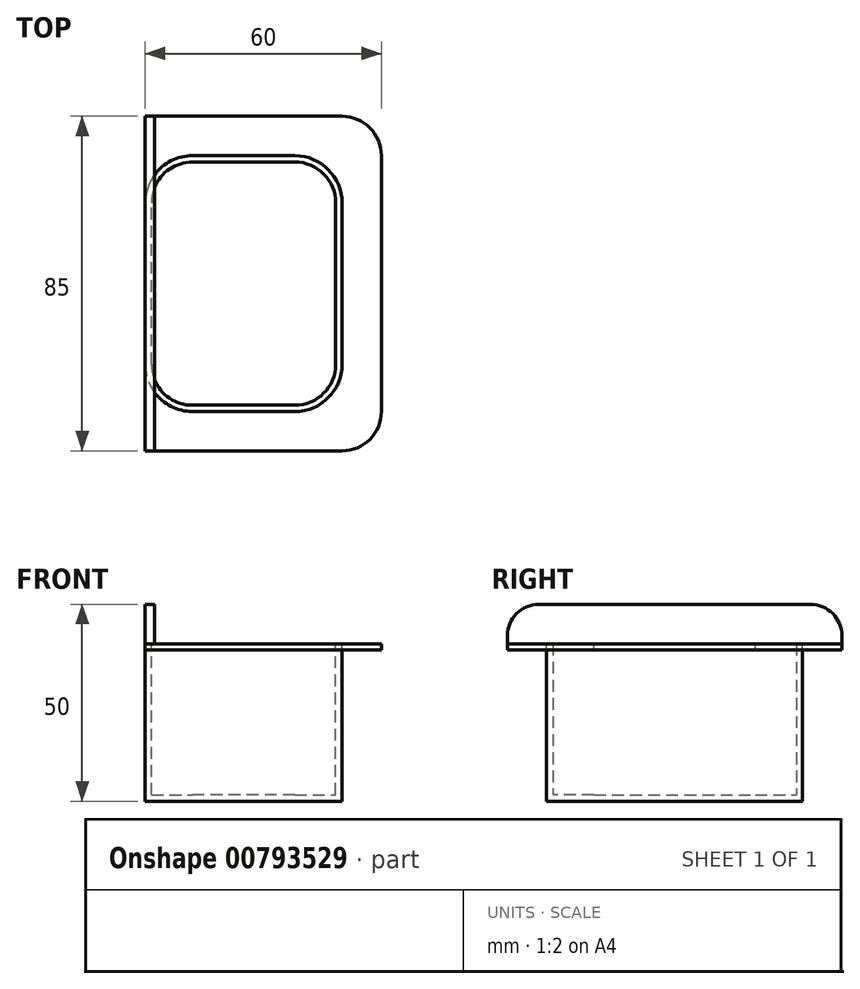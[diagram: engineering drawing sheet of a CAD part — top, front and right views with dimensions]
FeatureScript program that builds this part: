
annotation { "Feature Type Name" : "Feature", "Feature Type Description" : "" }
export const myFeature = defineFeature(function(context is Context, id is Id, definition is map)
    precondition{}
    {
        {
            var Q0;
            Q0=qCreatedBy(makeId("Top.planeOp"),FACE);
            var sketch = newSketch(context, id + "F0", { "sketchPlane" : qUnion([Q0])});
            skLineSegment(sketch, "E0.bottom", {"start": v(25, -32.5) * mm, "end": v(-25, -32.5) * mm});
            skLineSegment(sketch, "E0.top", {"start": v(25, 32.5) * mm, "end": v(-25, 32.5) * mm});
            skLineSegment(sketch, "E0.left", {"start": v(25, -32.5) * mm, "end": v(25, 32.5) * mm});
            skLineSegment(sketch, "E0.right", {"start": v(-25, -32.5) * mm, "end": v(-25, 32.5) * mm});
            skPoint(sketch, "E0.middle", {"position": v(0, 0) * mm});
            skSolve(sketch);
        }
        {
            var Q0;
            Q0 = qSketchRegion(id + "F0", true);
            extrude(context, id + "F1", {"entities" : qUnion([Q0]), "depth" : 40 * mm, "offsetDistance" : 25 * mm});
        }
        {
            var Q0;
            Q0=makeQuery(id+"F1.opExtrude","SWEPT_EDGE",EDGE,{"disambiguationData":[OSD([sQuery(id+"F0.wireOp",EDGE,"E0.bottom"),sQuery(id+"F0.wireOp",EDGE,"E0.right")])]});
            var Q1;
            Q1=makeQuery(id+"F1.opExtrude","SWEPT_EDGE",EDGE,{"disambiguationData":[OSD([sQuery(id+"F0.wireOp",EDGE,"E0.bottom"),sQuery(id+"F0.wireOp",EDGE,"E0.left")])]});
            var Q2;
            Q2=makeQuery(id+"F1.opExtrude","SWEPT_EDGE",EDGE,{"disambiguationData":[OSD([sQuery(id+"F0.wireOp",EDGE,"E0.top"),sQuery(id+"F0.wireOp",EDGE,"E0.left")])]});
            var Q3;
            Q3=makeQuery(id+"F1.opExtrude","SWEPT_EDGE",EDGE,{"disambiguationData":[OSD([sQuery(id+"F0.wireOp",EDGE,"E0.top"),sQuery(id+"F0.wireOp",EDGE,"E0.right")])]});
            fillet(context, id + "F2", {"entities" : qUnion([Q0, Q1, Q2, Q3]), "radius" : 12 * mm, "tangentPropagation" : true, "allowEdgeOverflow" : false});
        }
        {
            var Q0;
            Q0=makeQuery(id+"F1.opExtrude","CAP_FACE",FACE,{"disambiguationData":[OSD([sQuery(id+"F0.wireOp",EDGE,"E0.bottom"),sQuery(id+"F0.wireOp",EDGE,"E0.top"),sQuery(id+"F0.wireOp",EDGE,"E0.left"),sQuery(id+"F0.wireOp",EDGE,"E0.right")])],"isStart":false});
            shell(context, id + "F3", {"entities" : qUnion([Q0]), "thickness" : 1.6 * mm});
        }
        {
            var Q0;
            Q0=makeQuery(id+"F1.opExtrude","CAP_FACE",FACE,{"disambiguationData":[OSD([sQuery(id+"F0.wireOp",EDGE,"E0.bottom"),sQuery(id+"F0.wireOp",EDGE,"E0.top"),sQuery(id+"F0.wireOp",EDGE,"E0.left"),sQuery(id+"F0.wireOp",EDGE,"E0.right")])],"isStart":false});
            var sketch = newSketch(context, id + "F4", { "sketchPlane" : qUnion([Q0])});
            skLineSegment(sketch, "E1.bottom", {"start": v(-25, 42.5) * mm, "end": v(35, 42.5) * mm});
            skLineSegment(sketch, "E1.top", {"start": v(-25, -42.5) * mm, "end": v(35, -42.5) * mm});
            skLineSegment(sketch, "E1.left", {"start": v(-25, 42.5) * mm, "end": v(-25, -42.5) * mm});
            skLineSegment(sketch, "E1.right", {"start": v(35, 42.5) * mm, "end": v(35, -42.5) * mm});
            skSolve(sketch);
        }
        {
            var Q0;
            {var subQ7=sQuery(id+"F4.wireOp",EDGE,"E1.bottom");Q0=makeQuery(id+"F4.imprint","IMPRINT",FACE,{"disambiguationData":[TD([[makeQuery(id+"F4.imprint","IMPRINT",EDGE,{"derivedFrom":subQ7}),-1.0]])]});}
            extrude(context, id + "F5", {"entities" : qUnion([Q0]), "oppositeDirection" : true, "depth" : 1.6 * mm, "offsetDistance" : 25 * mm});
        }
        {
            var Q0;
            Q0=makeQuery(id+"F5.opExtrude","SWEPT_EDGE",EDGE,{"disambiguationData":[OSD([sQuery(id+"F4.wireOp",EDGE,"E1.bottom"),sQuery(id+"F4.wireOp",EDGE,"E1.right")])]});
            var Q1;
            Q1=makeQuery(id+"F5.opExtrude","SWEPT_EDGE",EDGE,{"disambiguationData":[OSD([sQuery(id+"F4.wireOp",EDGE,"E1.top"),sQuery(id+"F4.wireOp",EDGE,"E1.right")])]});
            fillet(context, id + "F6", {"entities" : qUnion([Q0, Q1]), "radius" : 10 * mm, "tangentPropagation" : true, "allowEdgeOverflow" : false});
        }
        {
            var Q0;
            Q0=makeQuery(id+"F5.opExtrude","CAP_FACE",FACE,{"disambiguationData":[OSD([sQuery(id+"F0.wireOp",EDGE,"E0.bottom"),sQuery(id+"F0.wireOp",EDGE,"E0.top"),sQuery(id+"F0.wireOp",EDGE,"E0.left"),sQuery(id+"F0.wireOp",EDGE,"E0.right"),sQuery(id+"F4.wireOp",EDGE,"E1.bottom"),sQuery(id+"F4.wireOp",EDGE,"E1.top"),sQuery(id+"F4.wireOp",EDGE,"E1.left"),sQuery(id+"F4.wireOp",EDGE,"E1.right")])],"isStart":true});
            var sketch = newSketch(context, id + "F7", { "sketchPlane" : qUnion([Q0])});
            skPoint(sketch, "E2.oppositeSnap0", {"position": v(-22.66, -30.16) * mm});
            skLineSegment(sketch, "E2.bottom", {"start": v(-25, 42.5) * mm, "end": v(-22.66, 42.5) * mm});
            skLineSegment(sketch, "E2.top", {"start": v(-25, -42.5) * mm, "end": v(-22.66, -42.5) * mm});
            skLineSegment(sketch, "E2.left", {"start": v(-25, 42.5) * mm, "end": v(-25, -42.5) * mm});
            skLineSegment(sketch, "E2.right", {"start": v(-22.66, 42.5) * mm, "end": v(-22.66, -42.5) * mm});
            skSolve(sketch);
        }
        {
            var Q0;
            Q0 = qSketchRegion(id + "F7", true);
            extrude(context, id + "F8", {"entities" : qUnion([Q0]), "depth" : 10 * mm, "offsetDistance" : 25 * mm});
        }
        {
            var Q0;
            Q0=makeQuery(id+"F8.opExtrude","CAP_EDGE",EDGE,{"disambiguationData":[OSD([sQuery(id+"F7.wireOp",EDGE,"E2.bottom")])],"isStart":false});
            var Q1;
            Q1=makeQuery(id+"F8.opExtrude","CAP_EDGE",EDGE,{"disambiguationData":[OSD([sQuery(id+"F7.wireOp",EDGE,"E2.top")])],"isStart":false});
            fillet(context, id + "F9", {"entities" : qUnion([Q0, Q1]), "radius" : 8 * mm, "tangentPropagation" : true, "allowEdgeOverflow" : false});
        }
    });
